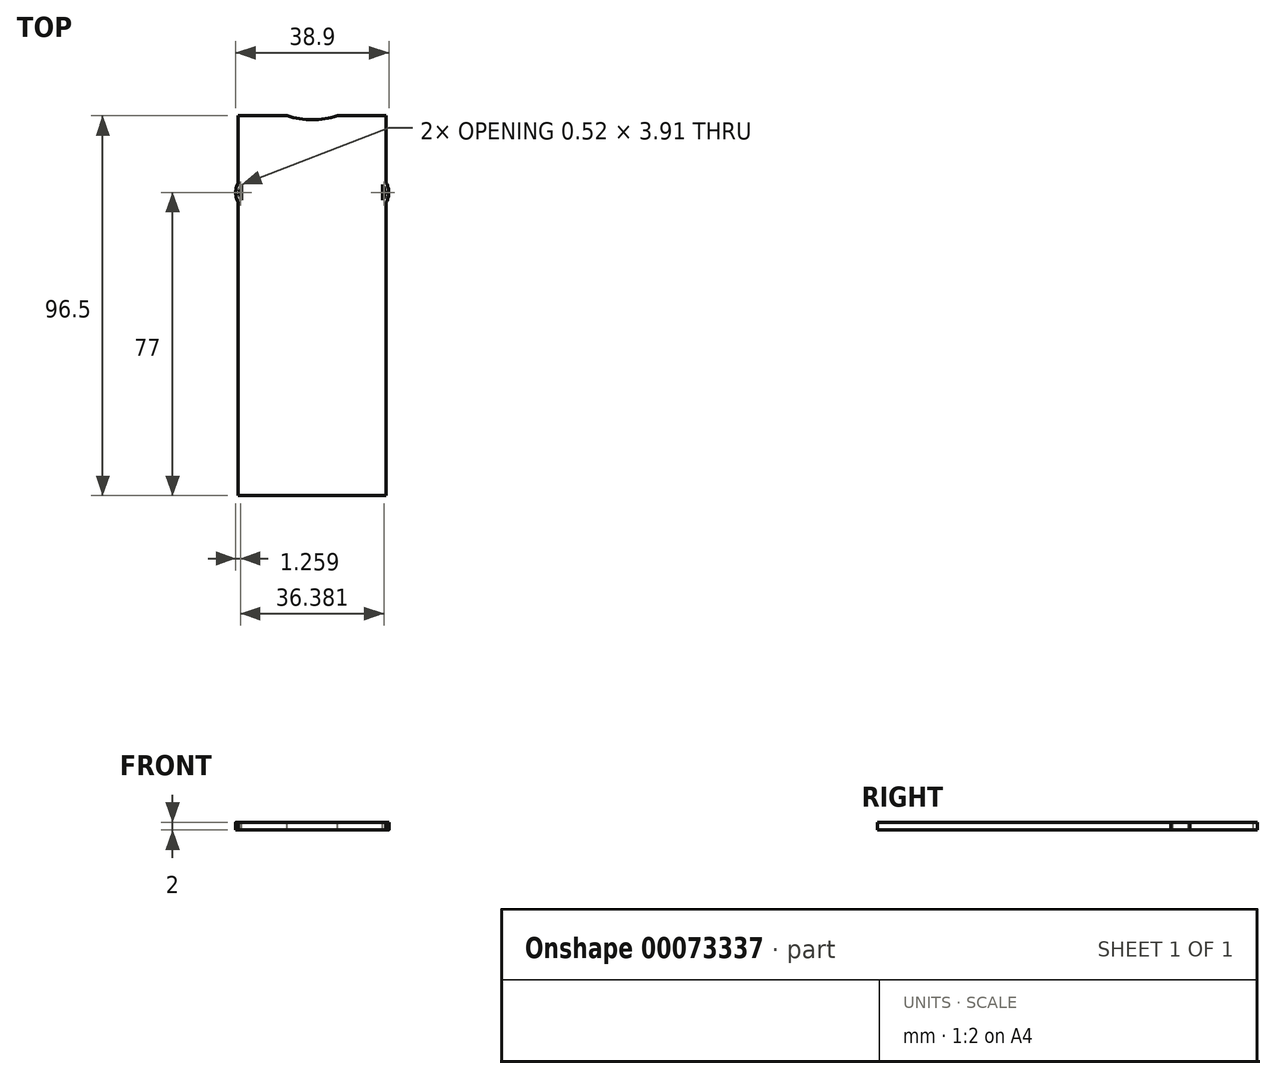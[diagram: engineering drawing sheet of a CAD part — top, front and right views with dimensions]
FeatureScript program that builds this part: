
annotation { "Feature Type Name" : "Feature", "Feature Type Description" : "" }
export const myFeature = defineFeature(function(context is Context, id is Id, definition is map)
    precondition{}
    {
        {
            var Q0;
            Q0=qCreatedBy(makeId("Top.planeOp"),FACE);
            var sketch = newSketch(context, id + "F0", { "sketchPlane" : qUnion([Q0])});
            skLineSegment(sketch, "E0.bottom", {"start": v(18.8, 48.25) * mm, "end": v(-18.8, 48.25) * mm});
            skLineSegment(sketch, "E0.top", {"start": v(18.8, -48.25) * mm, "end": v(-18.8, -48.25) * mm});
            skLineSegment(sketch, "E0.left", {"start": v(18.8, 48.25) * mm, "end": v(18.8, -48.25) * mm});
            skLineSegment(sketch, "E0.right", {"start": v(-18.8, 48.25) * mm, "end": v(-18.8, -48.25) * mm});
            skPoint(sketch, "E0.middle", {"position": v(0, 0) * mm});
            skSolve(sketch);
        }
        {
            var Q0;
            Q0=qSketchRegion(id+"F0",true);
            extrude(context, id + "F1", {"entities" : qUnion([Q0]), "depth" : 2 * mm});
        }
        {
            var Q0;
            Q0=makeQuery(id+"F1.opExtrude","CAP_FACE",FACE,{"disambiguationData":[OSD([sQuery(id+"F0.wireOp",EDGE,"E0.bottom"),sQuery(id+"F0.wireOp",EDGE,"E0.top"),sQuery(id+"F0.wireOp",EDGE,"E0.left"),sQuery(id+"F0.wireOp",EDGE,"E0.right")])],"isStart":false});
            var sketch = newSketch(context, id + "F2", { "sketchPlane" : qUnion([Q0])});
            skCircle(sketch, "E1", {"center": v(-14.5, 28.75) * mm, "radius": 4.95 * mm});
            skCircle(sketch, "E2", {"center": v(14.5, 28.75) * mm, "radius": 4.95 * mm});
            skLineSegment(sketch, "E3", {"start": v(-14.5, 28.75) * mm, "end": v(14.5, 28.75) * mm, "construction": true});
            skLineSegment(sketch, "E4", {"start": v(0, 28.75) * mm, "end": v(0, -48.25) * mm, "construction": true});
            skSolve(sketch);
        }
        {
            var Q0;
            {var subQ0=sQuery(id+"F2.wireOp",EDGE,"E1");var subQ1=makeQuery(id+"F1.opExtrude","CAP_EDGE",EDGE,{"disambiguationData":[OSD([sQuery(id+"F0.wireOp",EDGE,"E0.right")])],"isStart":false});var subQ2=makeQuery(id+"F2.imprint","INTERSECT",VERTEX,{"disambiguationData":[OD(0.0)],"derivedFrom":[subQ1,subQ0]});Q0=makeQuery(id+"F2.imprint","IMPRINT",FACE,{"disambiguationData":[TD([[makeQuery(id+"F2.imprint","IMPRINT",EDGE,{"disambiguationData":[TD([[subQ2,-1.0]])],"derivedFrom":subQ0}),1.0]])]});}
            var Q1;
            {var subQ0=sQuery(id+"F2.wireOp",EDGE,"E2");var subQ1=makeQuery(id+"F1.opExtrude","CAP_EDGE",EDGE,{"disambiguationData":[OSD([sQuery(id+"F0.wireOp",EDGE,"E0.left")])],"isStart":false});var subQ2=makeQuery(id+"F2.imprint","INTERSECT",VERTEX,{"disambiguationData":[OD(0.0)],"derivedFrom":[subQ1,subQ0]});Q1=makeQuery(id+"F2.imprint","IMPRINT",FACE,{"disambiguationData":[TD([[makeQuery(id+"F2.imprint","IMPRINT",EDGE,{"disambiguationData":[TD([[subQ2,1.0]])],"derivedFrom":subQ0}),1.0]])]});}
            var Q2;
            Q2=makeQuery(id+"F1.opExtrude","CAP_FACE",FACE,{"disambiguationData":[OSD([sQuery(id+"F0.wireOp",EDGE,"E0.bottom"),sQuery(id+"F0.wireOp",EDGE,"E0.top"),sQuery(id+"F0.wireOp",EDGE,"E0.left"),sQuery(id+"F0.wireOp",EDGE,"E0.right")])],"isStart":true});
            extrude(context, id + "F3", {"entities" : qUnion([Q0, Q1]), "operationType" : NewBodyOperationType.ADD, "endBound" : BoundingType.UP_TO_SURFACE, "oppositeDirection" : true, "endBoundEntityFace" : qUnion([Q2]), "depth" : 25 * mm});
        }
        {
            var Q0;
            {var subQ0=sQuery(id+"F0.wireOp",EDGE,"E0.left");var subQ1=sQuery(id+"F0.wireOp",EDGE,"E0.right");Q0=makeQuery(id+"F3.boolean.opBoolean","MERGE",FACE,{"derivedFrom":[makeQuery(id+"F1.opExtrude","CAP_FACE",FACE,{"disambiguationData":[OSD([sQuery(id+"F0.wireOp",EDGE,"E0.bottom"),sQuery(id+"F0.wireOp",EDGE,"E0.top"),subQ0,subQ1])],"isStart":false}),makeQuery(id+"F3.opExtrude","CAP_FACE",FACE,{"disambiguationData":[OSD([subQ1,sQuery(id+"F2.wireOp",EDGE,"E1")])],"isStart":true}),makeQuery(id+"F3.opExtrude","CAP_FACE",FACE,{"disambiguationData":[OSD([subQ0,sQuery(id+"F2.wireOp",EDGE,"E2")])],"isStart":true})]});}
            var sketch = newSketch(context, id + "F4", { "sketchPlane" : qUnion([Q0])});
            skArc(sketch, "E5.0", {"start": v(-17.93, 30.7) * mm, "mid": v(-18.45, 28.75) * mm, "end": v(-17.93, 26.8) * mm});
            skLineSegment(sketch, "E6", {"start": v(-17.93, 26.8) * mm, "end": v(-17.93, 30.7) * mm});
            skLineSegment(sketch, "E7", {"start": v(0, -48.25) * mm, "end": v(0, 48.25) * mm, "construction": true});
            skLineSegment(sketch, "E8.MirrorCS", {"start": v(17.93, 26.8) * mm, "end": v(17.93, 30.7) * mm});
            skArc(sketch, "E9.MirrorCS", {"start": v(17.93, 30.7) * mm, "mid": v(18.45, 28.75) * mm, "end": v(17.93, 26.8) * mm});
            skArc(sketch, "E10", {"start": v(-6.4, 48.25) * mm, "mid": v(0, 47.25) * mm, "end": v(6.4, 48.25) * mm});
            skPoint(sketch, "E11", {"position": v(0, 47.25) * mm});
            skLineSegment(sketch, "E12", {"start": v(-6.4, 48.25) * mm, "end": v(6.4, 48.25) * mm});
            skSolve(sketch);
        }
        {
            var Q0;
            Q0=qSketchRegion(id+"F4",true);
            extrude(context, id + "F5", {"entities" : qUnion([Q0]), "operationType" : NewBodyOperationType.REMOVE, "endBound" : BoundingType.THROUGH_ALL, "oppositeDirection" : true, "depth" : 25 * mm});
        }
    });
